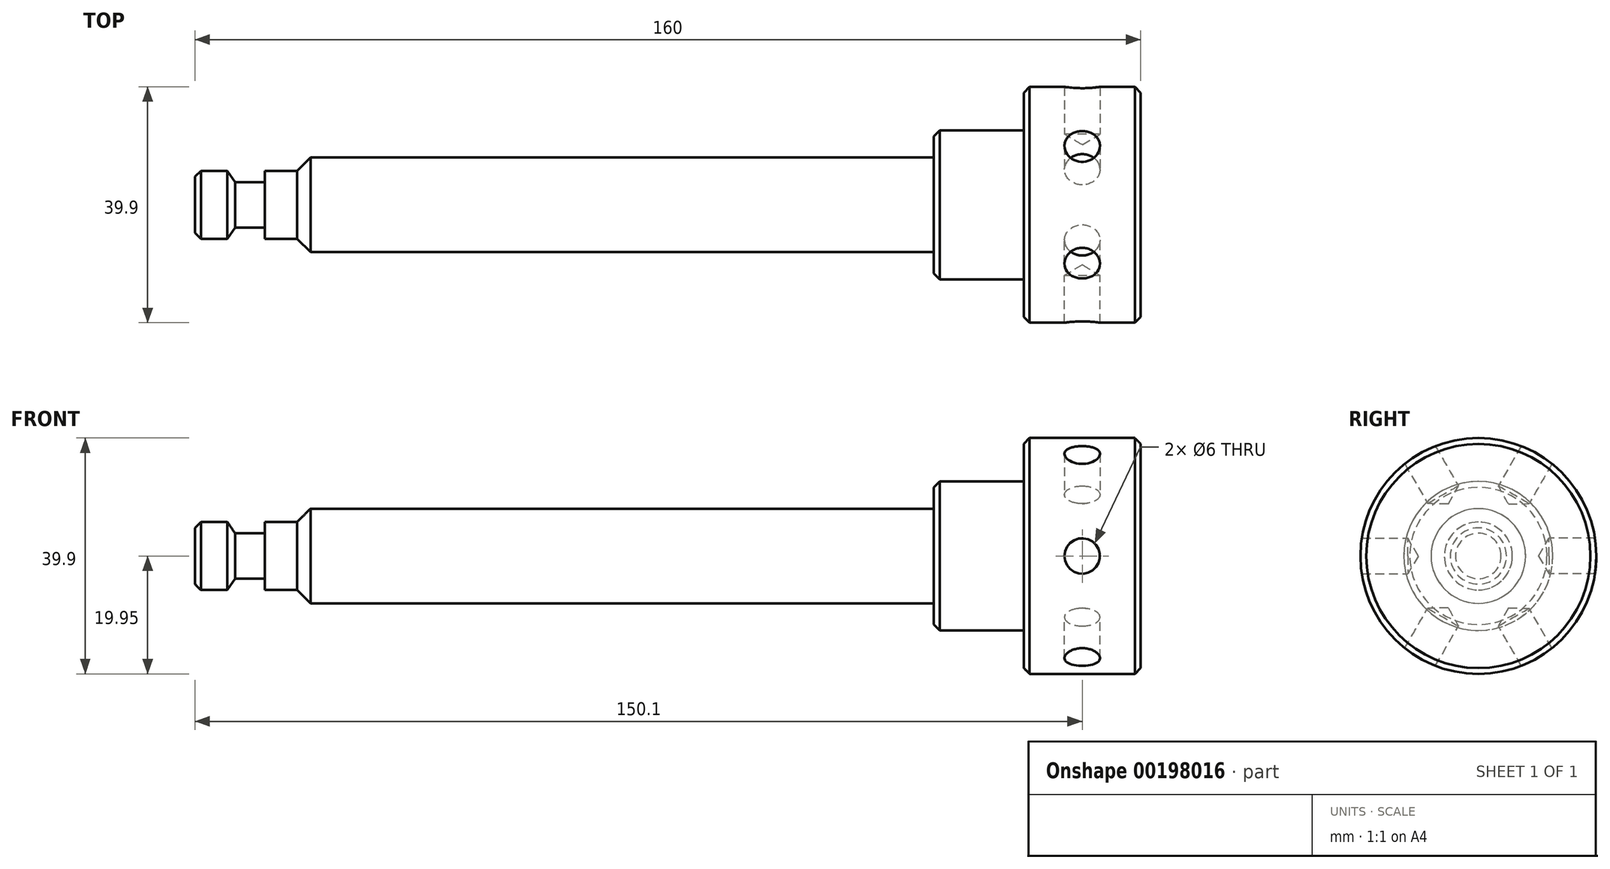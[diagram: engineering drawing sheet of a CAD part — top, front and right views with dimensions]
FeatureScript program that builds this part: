
annotation { "Feature Type Name" : "Feature", "Feature Type Description" : "" }
export const myFeature = defineFeature(function(context is Context, id is Id, definition is map)
    precondition{}
    {
        {
            var Q0;
            Q0=qCreatedBy(makeId("Top.planeOp"),FACE);
            var sketch = newSketch(context, id + "F0", { "sketchPlane" : qUnion([Q0])});
            skLineSegment(sketch, "E0", {"start": v(-0.14, 0) * mm, "end": v(-177.57, 0) * mm, "construction": true});
            skLineSegment(sketch, "E1", {"start": v(0, 0) * mm, "end": v(0, 19.95) * mm});
            skLineSegment(sketch, "E2", {"start": v(0, 19.95) * mm, "end": v(-19.8, 19.95) * mm});
            skLineSegment(sketch, "E3", {"start": v(-19.8, 19.95) * mm, "end": v(-19.8, 12.6) * mm});
            skLineSegment(sketch, "E4", {"start": v(-19.8, 12.6) * mm, "end": v(-35, 12.6) * mm});
            skLineSegment(sketch, "E5", {"start": v(-35, 12.6) * mm, "end": v(-35, 8) * mm});
            skLineSegment(sketch, "E6", {"start": v(-35, 8) * mm, "end": v(-142.7, 8) * mm});
            skLineSegment(sketch, "E7", {"start": v(-142.7, 8) * mm, "end": v(-142.7, 5.75) * mm});
            skLineSegment(sketch, "E8", {"start": v(-142.7, 5.75) * mm, "end": v(-148.2, 5.75) * mm});
            skLineSegment(sketch, "E9", {"start": v(-148.2, 5.75) * mm, "end": v(-148.2, 3.85) * mm});
            skLineSegment(sketch, "E10", {"start": v(-148.2, 3.85) * mm, "end": v(-153.2, 3.85) * mm});
            skLineSegment(sketch, "E11", {"start": v(-153.2, 3.85) * mm, "end": v(-154.5, 5.75) * mm});
            skLineSegment(sketch, "E12", {"start": v(-154.5, 5.75) * mm, "end": v(-160, 5.75) * mm});
            skLineSegment(sketch, "E13", {"start": v(-160, 5.75) * mm, "end": v(-160, 0) * mm});
            skLineSegment(sketch, "E14", {"start": v(-160, 0) * mm, "end": v(0, 0) * mm});
            skSolve(sketch);
        }
        {
            var Q0;
            Q0=makeQuery(id+"F0.imprint","IMPRINT",FACE,{"disambiguationData":[TD([[makeQuery(id+"F0.imprint","IMPRINT",EDGE,{"derivedFrom":sQuery(id+"F0.wireOp",EDGE,"E1")}),1.0]])]});
            var Q1;
            Q1=sQuery(id+"F0.wireOp",EDGE,"E14");
            revolve(context, id + "F1", {"entities" : qUnion([Q0]), "axis" : qUnion([Q1]), "revolveType" : RevolveType.FULL});
        }
        {
            var Q0;
            Q0=makeQuery(id+"F1.opRevolve","SWEPT_EDGE",EDGE,{"disambiguationData":[OSD([sQuery(id+"F0.wireOp",EDGE,"E12"),sQuery(id+"F0.wireOp",EDGE,"E13")])]});
            var Q1;
            Q1=makeQuery(id+"F1.opRevolve","SWEPT_EDGE",EDGE,{"disambiguationData":[OSD([sQuery(id+"F0.wireOp",EDGE,"E1"),sQuery(id+"F0.wireOp",EDGE,"E2")])]});
            var Q2;
            Q2=makeQuery(id+"F1.opRevolve","SWEPT_EDGE",EDGE,{"disambiguationData":[OSD([sQuery(id+"F0.wireOp",EDGE,"E4"),sQuery(id+"F0.wireOp",EDGE,"E5")])]});
            var Q3;
            Q3=makeQuery(id+"F1.opRevolve","SWEPT_EDGE",EDGE,{"disambiguationData":[OSD([sQuery(id+"F0.wireOp",EDGE,"E2"),sQuery(id+"F0.wireOp",EDGE,"E3")])]});
            chamfer(context, id + "F2", {"entities" : qUnion([Q0, Q1, Q2, Q3]), "width" : 1 * mm, "tangentPropagation" : true});
        }
        {
            var Q0;
            Q0=makeQuery(id+"F1.opRevolve","SWEPT_EDGE",EDGE,{"disambiguationData":[OSD([sQuery(id+"F0.wireOp",EDGE,"E6"),sQuery(id+"F0.wireOp",EDGE,"E7")])]});
            chamfer(context, id + "F3", {"entities" : qUnion([Q0]), "width" : 2.25 * mm, "tangentPropagation" : true});
        }
        {
            var Q0;
            Q0=makeQuery(id+"F1.opRevolve","SWEPT_FACE",FACE,{"disambiguationData":[OSD([sQuery(id+"F0.wireOp",EDGE,"E1")])]});
            var sketch = newSketch(context, id + "F4", { "sketchPlane" : qUnion([Q0])});
            skLineSegment(sketch, "E15", {"start": v(0, 0) * mm, "end": v(26.9, 0) * mm, "construction": true});
            skLineSegment(sketch, "E16", {"start": v(19.95, 12.37) * mm, "end": v(19.95, -12.53) * mm, "construction": true});
            skLineSegment(sketch, "E17.1.0", {"start": v(-0.74, 23.46) * mm, "end": v(20.82, 11.01) * mm, "construction": true});
            skLineSegment(sketch, "E17.1.1", {"start": v(0, 0) * mm, "end": v(13.45, 23.3) * mm, "construction": true});
            skLineSegment(sketch, "E17.2.0", {"start": v(-20.69, 11.1) * mm, "end": v(0.87, 23.54) * mm, "construction": true});
            skLineSegment(sketch, "E17.2.1", {"start": v(0, 0) * mm, "end": v(-13.45, 23.3) * mm, "construction": true});
            skLineSegment(sketch, "E17.3.0", {"start": v(-19.95, -12.37) * mm, "end": v(-19.95, 12.53) * mm, "construction": true});
            skLineSegment(sketch, "E17.3.1", {"start": v(0, 0) * mm, "end": v(-26.9, 0) * mm, "construction": true});
            skLineSegment(sketch, "E17.4.0", {"start": v(0.74, -23.46) * mm, "end": v(-20.82, -11.01) * mm, "construction": true});
            skLineSegment(sketch, "E17.4.1", {"start": v(0, 0) * mm, "end": v(-13.45, -23.3) * mm, "construction": true});
            skLineSegment(sketch, "E17.5.0", {"start": v(20.69, -11.1) * mm, "end": v(-0.87, -23.54) * mm, "construction": true});
            skLineSegment(sketch, "E17.5.1", {"start": v(0, 0) * mm, "end": v(13.45, -23.3) * mm, "construction": true});
            skPoint(sketch, "E17.center", {"position": v(0, 0) * mm});
            skSolve(sketch);
        }
        {
            var Q0;
            Q0=sQuery(id+"F4.wireOp",EDGE,"E16");
            cPlane(context, id + "F5", {"entities" : qUnion([Q0]), "cplaneType" : CPlaneType.LINE_ANGLE, "offset" : 25 * mm, "angle" : 90 * degree, "width" : 150 * mm, "height" : 150 * mm});
        }
        {
            var Q0;
            Q0=sQuery(id+"F4.wireOp",EDGE,"E17.1.0");
            cPlane(context, id + "F6", {"entities" : qUnion([Q0]), "cplaneType" : CPlaneType.LINE_ANGLE, "offset" : 25 * mm, "angle" : 0 * degree, "width" : 150 * mm, "height" : 150 * mm});
        }
        {
            var Q0;
            Q0=sQuery(id+"F4.wireOp",EDGE,"E17.2.0");
            cPlane(context, id + "F7", {"entities" : qUnion([Q0]), "cplaneType" : CPlaneType.LINE_ANGLE, "offset" : 25 * mm, "angle" : 0 * degree, "width" : 150 * mm, "height" : 150 * mm});
        }
        {
            var Q0;
            Q0=sQuery(id+"F4.wireOp",EDGE,"E17.3.0");
            cPlane(context, id + "F8", {"entities" : qUnion([Q0]), "cplaneType" : CPlaneType.LINE_ANGLE, "offset" : 25 * mm, "angle" : 90 * degree, "width" : 150 * mm, "height" : 150 * mm});
        }
        {
            var Q0;
            Q0=sQuery(id+"F4.wireOp",EDGE,"E17.4.0");
            cPlane(context, id + "F9", {"entities" : qUnion([Q0]), "cplaneType" : CPlaneType.LINE_ANGLE, "offset" : 25 * mm, "angle" : 0 * degree, "width" : 150 * mm, "height" : 150 * mm});
        }
        {
            var Q0;
            Q0=sQuery(id+"F4.wireOp",EDGE,"E17.5.0");
            cPlane(context, id + "F10", {"entities" : qUnion([Q0]), "cplaneType" : CPlaneType.LINE_ANGLE, "offset" : 25 * mm, "angle" : 0 * degree, "width" : 150 * mm, "height" : 150 * mm});
        }
        {
            var Q0;
            Q0=qCreatedBy(id+"F10.planeOp",FACE);
            var sketch = newSketch(context, id + "F11", { "sketchPlane" : qUnion([Q0])});
            skLineSegment(sketch, "E18", {"start": v(0, 0) * mm, "end": v(-24.04, 0) * mm, "construction": true});
            skPoint(sketch, "E19", {"position": v(-9.9, 0) * mm});
            skSolve(sketch);
        }
        {
            var Q0;
            Q0=qCreatedBy(id+"F9.planeOp",FACE);
            var sketch = newSketch(context, id + "F12", { "sketchPlane" : qUnion([Q0])});
            skLineSegment(sketch, "E20", {"start": v(0, 0) * mm, "end": v(-25.52, 0) * mm, "construction": true});
            skPoint(sketch, "E21", {"position": v(-9.9, 0) * mm});
            skSolve(sketch);
        }
        {
            var Q0;
            Q0=qCreatedBy(id+"F8.planeOp",FACE);
            var sketch = newSketch(context, id + "F13", { "sketchPlane" : qUnion([Q0])});
            skLineSegment(sketch, "E22", {"start": v(0, 0) * mm, "end": v(23.65, 0) * mm, "construction": true});
            skPoint(sketch, "E23", {"position": v(9.9, 0) * mm});
            skSolve(sketch);
        }
        {
            var Q0;
            Q0=qCreatedBy(id+"F7.planeOp",FACE);
            var sketch = newSketch(context, id + "F14", { "sketchPlane" : qUnion([Q0])});
            skLineSegment(sketch, "E24", {"start": v(0, 0) * mm, "end": v(-26.22, 0) * mm, "construction": true});
            skPoint(sketch, "E25", {"position": v(-9.9, 0) * mm});
            skSolve(sketch);
        }
        {
            var Q0;
            Q0=qCreatedBy(id+"F6.planeOp",FACE);
            var sketch = newSketch(context, id + "F15", { "sketchPlane" : qUnion([Q0])});
            skLineSegment(sketch, "E26", {"start": v(0, 0) * mm, "end": v(-33.74, 0) * mm, "construction": true});
            skPoint(sketch, "E27", {"position": v(-9.9, 0) * mm});
            skSolve(sketch);
        }
        {
            var Q0;
            Q0=qCreatedBy(id+"F5.planeOp",FACE);
            var sketch = newSketch(context, id + "F16", { "sketchPlane" : qUnion([Q0])});
            skLineSegment(sketch, "E28", {"start": v(0, 0) * mm, "end": v(19.8, 0) * mm, "construction": true});
            skPoint(sketch, "E29", {"position": v(9.9, 0) * mm});
            skSolve(sketch);
        }
        {
            var Q0;
            Q0=sQuery(id+"F13.wireOp",VERTEX,"E23");
            var Q1;
            Q1=makeQuery(id+"F1.opRevolve","SWEPT_BODY",BODY,{"disambiguationData":[OSD([sQuery(id+"F0.wireOp",EDGE,"E1"),sQuery(id+"F0.wireOp",EDGE,"E2"),sQuery(id+"F0.wireOp",EDGE,"E3"),sQuery(id+"F0.wireOp",EDGE,"E4"),sQuery(id+"F0.wireOp",EDGE,"E5"),sQuery(id+"F0.wireOp",EDGE,"E6"),sQuery(id+"F0.wireOp",EDGE,"E7"),sQuery(id+"F0.wireOp",EDGE,"E8"),sQuery(id+"F0.wireOp",EDGE,"E9"),sQuery(id+"F0.wireOp",EDGE,"E10"),sQuery(id+"F0.wireOp",EDGE,"E11"),sQuery(id+"F0.wireOp",EDGE,"E12"),sQuery(id+"F0.wireOp",EDGE,"E13"),sQuery(id+"F0.wireOp",EDGE,"E14")])]});
            hole(context, id + "F17", {"style" : HoleStyle.SIMPLE, "endStyle" : HoleEndStyle.BLIND, "oppositeDirection" : true, "holeDiameter" : 6 * mm, "holeDepth" : 8 * mm, "locations" : qUnion([Q0]), "scope" : qUnion([Q1]), "startStyle" : HoleStartStyle.SKETCH});
        }
        {
            var Q0;
            Q0=sQuery(id+"F14.wireOp",VERTEX,"E25");
            var Q1;
            Q1=makeQuery(id+"F1.opRevolve","SWEPT_BODY",BODY,{"disambiguationData":[OSD([sQuery(id+"F0.wireOp",EDGE,"E1"),sQuery(id+"F0.wireOp",EDGE,"E2"),sQuery(id+"F0.wireOp",EDGE,"E3"),sQuery(id+"F0.wireOp",EDGE,"E4"),sQuery(id+"F0.wireOp",EDGE,"E5"),sQuery(id+"F0.wireOp",EDGE,"E6"),sQuery(id+"F0.wireOp",EDGE,"E7"),sQuery(id+"F0.wireOp",EDGE,"E8"),sQuery(id+"F0.wireOp",EDGE,"E9"),sQuery(id+"F0.wireOp",EDGE,"E10"),sQuery(id+"F0.wireOp",EDGE,"E11"),sQuery(id+"F0.wireOp",EDGE,"E12"),sQuery(id+"F0.wireOp",EDGE,"E13"),sQuery(id+"F0.wireOp",EDGE,"E14")])]});
            hole(context, id + "F18", {"style" : HoleStyle.SIMPLE, "endStyle" : HoleEndStyle.BLIND, "holeDiameter" : 6 * mm, "holeDepth" : 8 * mm, "locations" : qUnion([Q0]), "scope" : qUnion([Q1]), "startStyle" : HoleStartStyle.SKETCH});
        }
        {
            var Q0;
            Q0=sQuery(id+"F15.wireOp",VERTEX,"E27");
            var Q1;
            Q1=makeQuery(id+"F1.opRevolve","SWEPT_BODY",BODY,{"disambiguationData":[OSD([sQuery(id+"F0.wireOp",EDGE,"E1"),sQuery(id+"F0.wireOp",EDGE,"E2"),sQuery(id+"F0.wireOp",EDGE,"E3"),sQuery(id+"F0.wireOp",EDGE,"E4"),sQuery(id+"F0.wireOp",EDGE,"E5"),sQuery(id+"F0.wireOp",EDGE,"E6"),sQuery(id+"F0.wireOp",EDGE,"E7"),sQuery(id+"F0.wireOp",EDGE,"E8"),sQuery(id+"F0.wireOp",EDGE,"E9"),sQuery(id+"F0.wireOp",EDGE,"E10"),sQuery(id+"F0.wireOp",EDGE,"E11"),sQuery(id+"F0.wireOp",EDGE,"E12"),sQuery(id+"F0.wireOp",EDGE,"E13"),sQuery(id+"F0.wireOp",EDGE,"E14")])]});
            hole(context, id + "F19", {"style" : HoleStyle.SIMPLE, "endStyle" : HoleEndStyle.BLIND, "holeDiameter" : 6 * mm, "holeDepth" : 8 * mm, "locations" : qUnion([Q0]), "scope" : qUnion([Q1]), "startStyle" : HoleStartStyle.SKETCH});
        }
        {
            var Q0;
            Q0=sQuery(id+"F16.wireOp",VERTEX,"E29");
            var Q1;
            Q1=makeQuery(id+"F1.opRevolve","SWEPT_BODY",BODY,{"disambiguationData":[OSD([sQuery(id+"F0.wireOp",EDGE,"E1"),sQuery(id+"F0.wireOp",EDGE,"E2"),sQuery(id+"F0.wireOp",EDGE,"E3"),sQuery(id+"F0.wireOp",EDGE,"E4"),sQuery(id+"F0.wireOp",EDGE,"E5"),sQuery(id+"F0.wireOp",EDGE,"E6"),sQuery(id+"F0.wireOp",EDGE,"E7"),sQuery(id+"F0.wireOp",EDGE,"E8"),sQuery(id+"F0.wireOp",EDGE,"E9"),sQuery(id+"F0.wireOp",EDGE,"E10"),sQuery(id+"F0.wireOp",EDGE,"E11"),sQuery(id+"F0.wireOp",EDGE,"E12"),sQuery(id+"F0.wireOp",EDGE,"E13"),sQuery(id+"F0.wireOp",EDGE,"E14")])]});
            hole(context, id + "F20", {"style" : HoleStyle.SIMPLE, "endStyle" : HoleEndStyle.BLIND, "holeDiameter" : 6 * mm, "holeDepth" : 8 * mm, "locations" : qUnion([Q0]), "scope" : qUnion([Q1]), "startStyle" : HoleStartStyle.SKETCH});
        }
        {
            var Q0;
            Q0=sQuery(id+"F11.wireOp",VERTEX,"E19");
            var Q1;
            Q1=makeQuery(id+"F1.opRevolve","SWEPT_BODY",BODY,{"disambiguationData":[OSD([sQuery(id+"F0.wireOp",EDGE,"E1"),sQuery(id+"F0.wireOp",EDGE,"E2"),sQuery(id+"F0.wireOp",EDGE,"E3"),sQuery(id+"F0.wireOp",EDGE,"E4"),sQuery(id+"F0.wireOp",EDGE,"E5"),sQuery(id+"F0.wireOp",EDGE,"E6"),sQuery(id+"F0.wireOp",EDGE,"E7"),sQuery(id+"F0.wireOp",EDGE,"E8"),sQuery(id+"F0.wireOp",EDGE,"E9"),sQuery(id+"F0.wireOp",EDGE,"E10"),sQuery(id+"F0.wireOp",EDGE,"E11"),sQuery(id+"F0.wireOp",EDGE,"E12"),sQuery(id+"F0.wireOp",EDGE,"E13"),sQuery(id+"F0.wireOp",EDGE,"E14")])]});
            hole(context, id + "F21", {"style" : HoleStyle.SIMPLE, "endStyle" : HoleEndStyle.BLIND, "holeDiameter" : 6 * mm, "holeDepth" : 8 * mm, "locations" : qUnion([Q0]), "scope" : qUnion([Q1]), "startStyle" : HoleStartStyle.SKETCH});
        }
        {
            var Q0;
            Q0=sQuery(id+"F12.wireOp",VERTEX,"E21");
            var Q1;
            Q1=makeQuery(id+"F1.opRevolve","SWEPT_BODY",BODY,{"disambiguationData":[OSD([sQuery(id+"F0.wireOp",EDGE,"E1"),sQuery(id+"F0.wireOp",EDGE,"E2"),sQuery(id+"F0.wireOp",EDGE,"E3"),sQuery(id+"F0.wireOp",EDGE,"E4"),sQuery(id+"F0.wireOp",EDGE,"E5"),sQuery(id+"F0.wireOp",EDGE,"E6"),sQuery(id+"F0.wireOp",EDGE,"E7"),sQuery(id+"F0.wireOp",EDGE,"E8"),sQuery(id+"F0.wireOp",EDGE,"E9"),sQuery(id+"F0.wireOp",EDGE,"E10"),sQuery(id+"F0.wireOp",EDGE,"E11"),sQuery(id+"F0.wireOp",EDGE,"E12"),sQuery(id+"F0.wireOp",EDGE,"E13"),sQuery(id+"F0.wireOp",EDGE,"E14")])]});
            hole(context, id + "F22", {"style" : HoleStyle.SIMPLE, "endStyle" : HoleEndStyle.BLIND, "holeDiameter" : 6 * mm, "holeDepth" : 8 * mm, "locations" : qUnion([Q0]), "scope" : qUnion([Q1]), "startStyle" : HoleStartStyle.SKETCH});
        }
    });
